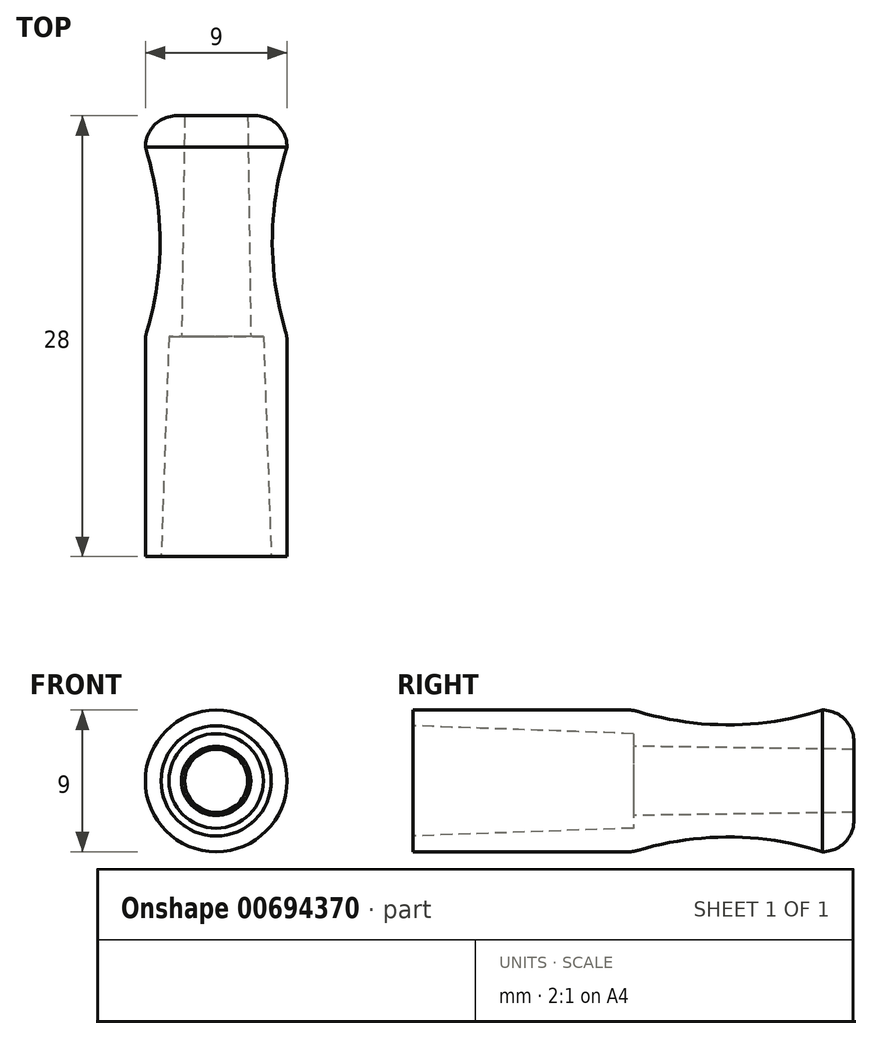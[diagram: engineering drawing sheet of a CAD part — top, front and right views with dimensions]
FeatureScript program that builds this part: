
annotation { "Feature Type Name" : "Feature", "Feature Type Description" : "" }
export const myFeature = defineFeature(function(context is Context, id is Id, definition is map)
    precondition{}
    {
        {
            var Q0;
            Q0=qCreatedBy(makeId("Right.planeOp"),FACE);
            var sketch = newSketch(context, id + "F0", { "sketchPlane" : qUnion([Q0])});
            skLineSegment(sketch, "E0", {"start": v(0, -4.5) * mm, "end": v(-2, -4.5) * mm});
            skArc(sketch, "E1", {"start": v(-2, -4.5) * mm, "mid": v(-8, -3.57) * mm, "end": v(-14, -4.5) * mm});
            skLineSegment(sketch, "E2", {"start": v(-14, -4.5) * mm, "end": v(-28, -4.5) * mm});
            skLineSegment(sketch, "E3", {"start": v(0, -2) * mm, "end": v(0, -4.5) * mm});
            skLineSegment(sketch, "E4", {"start": v(0, -2) * mm, "end": v(-14, -2.2) * mm});
            skLineSegment(sketch, "E5", {"start": v(-14, -3) * mm, "end": v(-14, -2.2) * mm});
            skLineSegment(sketch, "E6", {"start": v(-28, -4.5) * mm, "end": v(-28, -3.5) * mm});
            skLineSegment(sketch, "E7", {"start": v(0, 0) * mm, "end": v(-31.98, 0) * mm, "construction": true});
            skLineSegment(sketch, "E8", {"start": v(-28, -3.5) * mm, "end": v(-14, -3) * mm});
            skSolve(sketch);
        }
        {
            var Q0;
            Q0=makeQuery(id+"F0.imprint","IMPRINT",FACE,{"disambiguationData":[TD([[makeQuery(id+"F0.imprint","IMPRINT",EDGE,{"derivedFrom":sQuery(id+"F0.wireOp",EDGE,"E0")}),-1.0]])]});
            var Q1;
            Q1=sQuery(id+"F0.wireOp",EDGE,"E7");
            revolve(context, id + "F1", {"entities" : qUnion([Q0]), "axis" : qUnion([Q1]), "revolveType" : RevolveType.FULL});
        }
        {
            var Q0;
            Q0=makeQuery(id+"F1.opRevolve","SWEPT_EDGE",EDGE,{"disambiguationData":[OSD([sQuery(id+"F0.wireOp",EDGE,"E0"),sQuery(id+"F0.wireOp",EDGE,"E3")])]});
            fillet(context, id + "F2", {"entities" : qUnion([Q0]), "radius" : 2 * mm, "tangentPropagation" : true, "allowEdgeOverflow" : false});
        }
        {
            var Q0;
            Q0=makeQuery(id+"F1.opRevolve","SWEPT_EDGE",EDGE,{"disambiguationData":[OSD([sQuery(id+"F0.wireOp",EDGE,"E1"),sQuery(id+"F0.wireOp",EDGE,"E2")])]});
            fillet(context, id + "F3", {"entities" : qUnion([Q0]), "radius" : 2 * mm, "tangentPropagation" : true, "allowEdgeOverflow" : false});
        }
    });
